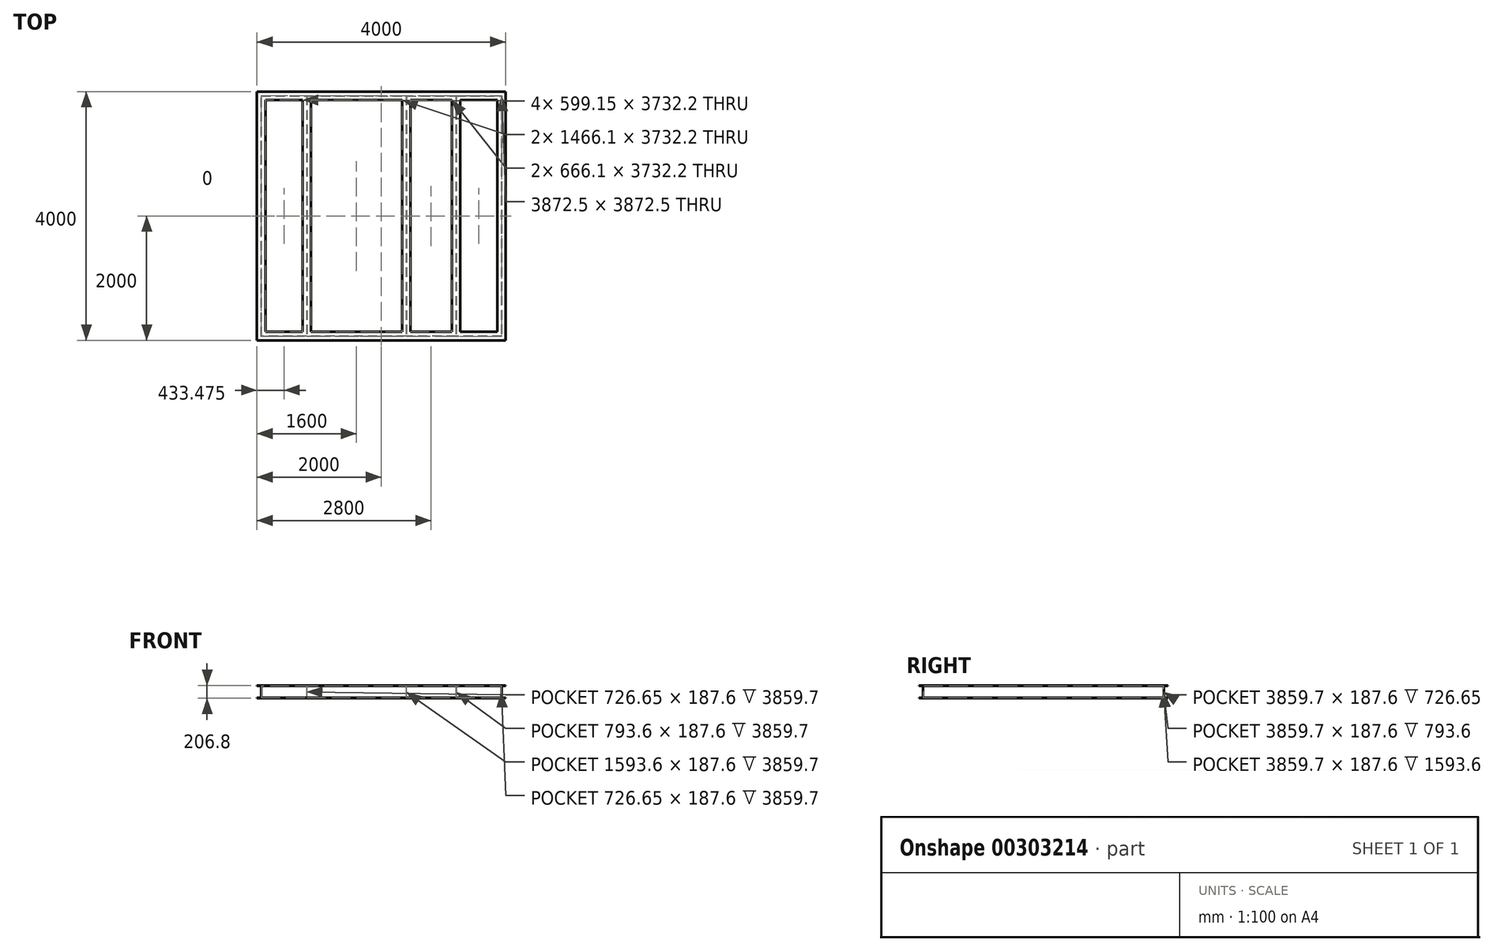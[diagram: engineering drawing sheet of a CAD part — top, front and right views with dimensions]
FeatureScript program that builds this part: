
annotation { "Feature Type Name" : "Feature", "Feature Type Description" : "" }
export const myFeature = defineFeature(function(context is Context, id is Id, definition is map)
    precondition{}
    {
        {
            var Q0;
            Q0=qCreatedBy(makeId("Top.planeOp"),FACE);
            var sketch = newSketch(context, id + "F0", { "sketchPlane" : qUnion([Q0])});
            skCircle(sketch, "E0", {"center": v(0, 0) * mm, "radius": 1985 * mm});
            skLineSegment(sketch, "E1.bottom", {"start": v(-1933.05, 1933.05) * mm, "end": v(1933.05, 1933.05) * mm});
            skLineSegment(sketch, "E1.top", {"start": v(-1933.05, -1933.05) * mm, "end": v(1933.05, -1933.05) * mm});
            skLineSegment(sketch, "E1.left", {"start": v(-1933.05, 1933.05) * mm, "end": v(-1933.05, -1933.05) * mm});
            skLineSegment(sketch, "E1.right", {"start": v(1933.05, 1933.05) * mm, "end": v(1933.05, -1933.05) * mm});
            skLineSegment(sketch, "E2", {"start": v(-1200, -1933.05) * mm, "end": v(-1200, 1933.05) * mm});
            skLineSegment(sketch, "E3", {"start": v(-400, -1933.05) * mm, "end": v(-400, 1933.05) * mm});
            skLineSegment(sketch, "E4", {"start": v(1200, -1933.05) * mm, "end": v(1200, 1933.05) * mm});
            skLineSegment(sketch, "E5", {"start": v(400, -1933.05) * mm, "end": v(400, 1933.05) * mm});
            skSolve(sketch);
        }
        {
            var Q0;
            Q0=qCreatedBy(makeId("Front.planeOp"),FACE);
            var sketch = newSketch(context, id + "F1", { "sketchPlane" : qUnion([Q0])});
            skLineSegment(sketch, "E6.bottom", {"start": v(1866.1, 103.4) * mm, "end": v(2000, 103.4) * mm});
            skLineSegment(sketch, "E6.top", {"start": v(1866.1, -103.4) * mm, "end": v(2000, -103.4) * mm});
            skLineSegment(sketch, "E6.left", {"start": v(1866.1, 103.4) * mm, "end": v(1866.1, 93.8) * mm});
            skLineSegment(sketch, "E6.right", {"start": v(2000, 103.4) * mm, "end": v(2000, 93.8) * mm});
            skLineSegment(sketch, "E7", {"start": v(1866.1, 93.8) * mm, "end": v(1929.85, 93.8) * mm});
            skLineSegment(sketch, "E8", {"start": v(1866.1, -93.8) * mm, "end": v(1929.85, -93.8) * mm});
            skLineSegment(sketch, "E9.left", {"start": v(1929.85, 93.8) * mm, "end": v(1929.85, -93.8) * mm});
            skLineSegment(sketch, "E9.right", {"start": v(1936.25, 93.8) * mm, "end": v(1936.25, -93.8) * mm});
            skLineSegment(sketch, "E10.trimOffspring", {"start": v(1936.25, -93.8) * mm, "end": v(2000, -93.8) * mm});
            skLineSegment(sketch, "E11.trimOffspring", {"start": v(2000, -93.8) * mm, "end": v(2000, -103.4) * mm});
            skLineSegment(sketch, "E12.trimOffspring", {"start": v(1866.1, -93.8) * mm, "end": v(1866.1, -103.4) * mm});
            skLineSegment(sketch, "E13.trimOffspring", {"start": v(1936.25, 93.8) * mm, "end": v(2000, 93.8) * mm});
            skLineSegment(sketch, "E14.1.0.0", {"start": v(1046.1, 103.4) * mm, "end": v(1180, 103.4) * mm});
            skLineSegment(sketch, "E14.1.0.1", {"start": v(1116.25, 93.8) * mm, "end": v(1116.25, -93.8) * mm});
            skLineSegment(sketch, "E14.1.0.2", {"start": v(1046.1, -93.8) * mm, "end": v(1109.85, -93.8) * mm});
            skLineSegment(sketch, "E14.1.0.3", {"start": v(1116.25, -93.8) * mm, "end": v(1180, -93.8) * mm});
            skLineSegment(sketch, "E14.1.0.4", {"start": v(1046.1, -103.4) * mm, "end": v(1180, -103.4) * mm});
            skLineSegment(sketch, "E14.1.0.5", {"start": v(1116.25, 93.8) * mm, "end": v(1180, 93.8) * mm});
            skLineSegment(sketch, "E14.1.0.6", {"start": v(1046.1, 93.8) * mm, "end": v(1109.85, 93.8) * mm});
            skLineSegment(sketch, "E14.1.0.7", {"start": v(1109.85, 93.8) * mm, "end": v(1109.85, -93.8) * mm});
            skLineSegment(sketch, "E14.1.0.8", {"start": v(1180, 103.4) * mm, "end": v(1180, 93.8) * mm});
            skLineSegment(sketch, "E14.1.0.9", {"start": v(1046.1, -93.8) * mm, "end": v(1046.1, -103.4) * mm});
            skLineSegment(sketch, "E14.1.0.10", {"start": v(1046.1, 103.4) * mm, "end": v(1046.1, 93.8) * mm});
            skLineSegment(sketch, "E14.1.0.11", {"start": v(1180, -93.8) * mm, "end": v(1180, -103.4) * mm});
            skLineSegment(sketch, "E14.2.0.0", {"start": v(226.1, 103.4) * mm, "end": v(360, 103.4) * mm});
            skLineSegment(sketch, "E14.2.0.1", {"start": v(296.25, 93.8) * mm, "end": v(296.25, -93.8) * mm});
            skLineSegment(sketch, "E14.2.0.2", {"start": v(226.1, -93.8) * mm, "end": v(289.85, -93.8) * mm});
            skLineSegment(sketch, "E14.2.0.3", {"start": v(296.25, -93.8) * mm, "end": v(360, -93.8) * mm});
            skLineSegment(sketch, "E14.2.0.4", {"start": v(226.1, -103.4) * mm, "end": v(360, -103.4) * mm});
            skLineSegment(sketch, "E14.2.0.5", {"start": v(296.25, 93.8) * mm, "end": v(360, 93.8) * mm});
            skLineSegment(sketch, "E14.2.0.6", {"start": v(226.1, 93.8) * mm, "end": v(289.85, 93.8) * mm});
            skLineSegment(sketch, "E14.2.0.7", {"start": v(289.85, 93.8) * mm, "end": v(289.85, -93.8) * mm});
            skLineSegment(sketch, "E14.2.0.8", {"start": v(360, 103.4) * mm, "end": v(360, 93.8) * mm});
            skLineSegment(sketch, "E14.2.0.9", {"start": v(226.1, -93.8) * mm, "end": v(226.1, -103.4) * mm});
            skLineSegment(sketch, "E14.2.0.10", {"start": v(226.1, 103.4) * mm, "end": v(226.1, 93.8) * mm});
            skLineSegment(sketch, "E14.2.0.11", {"start": v(360, -93.8) * mm, "end": v(360, -103.4) * mm});
            skLineSegment(sketch, "E14.direction1", {"start": v(1866.1, -93.8) * mm, "end": v(1046.1, -93.8) * mm, "construction": true});
            skSolve(sketch);
        }
        {
            var Q0;
            Q0=makeQuery(id+"F1.imprint","IMPRINT",FACE,{"disambiguationData":[TD([[makeQuery(id+"F1.imprint","IMPRINT",EDGE,{"derivedFrom":sQuery(id+"F1.wireOp",EDGE,"E6.bottom")}),-1.0]])]});
            var Q1;
            Q1=sQuery(id+"F0.wireOp",EDGE,"E1.top");
            var Q2;
            Q2=sQuery(id+"F0.wireOp",EDGE,"E1.right");
            var Q3;
            Q3=sQuery(id+"F0.wireOp",EDGE,"E1.left");
            var Q4;
            Q4=sQuery(id+"F0.wireOp",EDGE,"E1.bottom");
            sweep(context, id + "F2", {"profiles" : qUnion([Q0]), "path" : qUnion([Q1, Q2, Q3, Q4])});
        }
        {
            var Q0;
            Q0=makeQuery(id+"F2.opSweep","SWEPT_FACE",FACE,{"disambiguationData":[OSD([sQuery(id+"F0.wireOp",EDGE,"E1.bottom"),sQuery(id+"F1.wireOp",EDGE,"E9.right")])]});
            cPlane(context, id + "F3", {"entities" : qUnion([Q0]), "cplaneType" : CPlaneType.OFFSET, "offset" : 3.2 * mm, "oppositeDirection" : true, "width" : 150 * mm, "height" : 150 * mm});
        }
        {
            var Q0;
            Q0=qCreatedBy(id+"F3.planeOp",FACE);
            var sketch = newSketch(context, id + "F4", { "sketchPlane" : qUnion([Q0])});
            skLineSegment(sketch, "E15.bottom", {"start": v(-1866.1, 103.4) * mm, "end": v(-2000, 103.4) * mm});
            skLineSegment(sketch, "E15.top", {"start": v(-1866.1, -103.4) * mm, "end": v(-2000, -103.4) * mm});
            skLineSegment(sketch, "E15.left", {"start": v(-1866.1, 103.4) * mm, "end": v(-1866.1, 93.8) * mm});
            skLineSegment(sketch, "E15.right", {"start": v(-2000, 103.4) * mm, "end": v(-2000, 93.8) * mm});
            skLineSegment(sketch, "E16.bottom", {"start": v(-2000, 103.4) * mm, "end": v(-1866.1, 103.4) * mm});
            skLineSegment(sketch, "E16.top", {"start": v(-2000, 93.8) * mm, "end": v(-1936.25, 93.8) * mm});
            skLineSegment(sketch, "E17.left", {"start": v(-1929.85, 93.8) * mm, "end": v(-1929.85, -93.8) * mm});
            skLineSegment(sketch, "E17.right", {"start": v(-1936.25, 93.8) * mm, "end": v(-1936.25, -93.8) * mm});
            skLineSegment(sketch, "E18.bottom", {"start": v(-2000, -93.8) * mm, "end": v(-1936.25, -93.8) * mm});
            skLineSegment(sketch, "E18.top", {"start": v(-2000, -103.4) * mm, "end": v(-1866.1, -103.4) * mm});
            skLineSegment(sketch, "E18.left", {"start": v(-2000, -93.8) * mm, "end": v(-2000, -103.4) * mm});
            skLineSegment(sketch, "E18.right", {"start": v(-1866.1, -93.8) * mm, "end": v(-1866.1, -103.4) * mm});
            skLineSegment(sketch, "E19.trimOffspring", {"start": v(-1929.85, -93.8) * mm, "end": v(-1866.1, -93.8) * mm});
            skLineSegment(sketch, "E20.trimOffspring", {"start": v(-1929.85, 93.8) * mm, "end": v(-1866.1, 93.8) * mm});
            skLineSegment(sketch, "E21.1.0.0", {"start": v(-1266.95, 103.4) * mm, "end": v(-1133.05, 103.4) * mm});
            skLineSegment(sketch, "E21.1.0.1", {"start": v(-1203.2, 93.8) * mm, "end": v(-1203.2, -93.8) * mm});
            skLineSegment(sketch, "E21.1.0.2", {"start": v(-1196.8, 93.8) * mm, "end": v(-1196.8, -93.8) * mm});
            skLineSegment(sketch, "E21.1.0.3", {"start": v(-1266.95, 93.8) * mm, "end": v(-1203.2, 93.8) * mm});
            skLineSegment(sketch, "E21.1.0.4", {"start": v(-1266.95, 103.4) * mm, "end": v(-1266.95, 93.8) * mm});
            skLineSegment(sketch, "E21.1.0.5", {"start": v(-1133.05, 103.4) * mm, "end": v(-1133.05, 93.8) * mm});
            skLineSegment(sketch, "E21.1.0.6", {"start": v(-1196.8, 93.8) * mm, "end": v(-1133.05, 93.8) * mm});
            skLineSegment(sketch, "E21.1.0.7", {"start": v(-1196.8, -93.8) * mm, "end": v(-1133.05, -93.8) * mm});
            skLineSegment(sketch, "E21.1.0.8", {"start": v(-1133.05, -93.8) * mm, "end": v(-1133.05, -103.4) * mm});
            skLineSegment(sketch, "E21.1.0.9", {"start": v(-1266.95, -103.4) * mm, "end": v(-1133.05, -103.4) * mm});
            skLineSegment(sketch, "E21.1.0.10", {"start": v(-1266.95, -93.8) * mm, "end": v(-1266.95, -103.4) * mm});
            skLineSegment(sketch, "E21.1.0.11", {"start": v(-1266.95, -93.8) * mm, "end": v(-1203.2, -93.8) * mm});
            skLineSegment(sketch, "E21.direction1", {"start": v(-2000, 103.4) * mm, "end": v(-1266.95, 103.4) * mm, "construction": true});
            skLineSegment(sketch, "E22.1.0.0", {"start": v(-466.95, -103.4) * mm, "end": v(-333.05, -103.4) * mm});
            skLineSegment(sketch, "E22.1.0.1", {"start": v(-396.8, 93.8) * mm, "end": v(-396.8, -93.8) * mm});
            skLineSegment(sketch, "E22.1.0.2", {"start": v(-466.95, 103.4) * mm, "end": v(266.1, 103.4) * mm, "construction": true});
            skLineSegment(sketch, "E22.1.0.3", {"start": v(-396.8, 93.8) * mm, "end": v(-333.05, 93.8) * mm});
            skLineSegment(sketch, "E22.1.0.4", {"start": v(-396.8, -93.8) * mm, "end": v(-333.05, -93.8) * mm});
            skLineSegment(sketch, "E22.1.0.5", {"start": v(-403.2, 93.8) * mm, "end": v(-403.2, -93.8) * mm});
            skLineSegment(sketch, "E22.1.0.6", {"start": v(-466.95, -93.8) * mm, "end": v(-403.2, -93.8) * mm});
            skLineSegment(sketch, "E22.1.0.7", {"start": v(-466.95, 93.8) * mm, "end": v(-403.2, 93.8) * mm});
            skLineSegment(sketch, "E22.1.0.8", {"start": v(-466.95, 103.4) * mm, "end": v(-333.05, 103.4) * mm});
            skLineSegment(sketch, "E22.1.0.9", {"start": v(-333.05, -103.4) * mm, "end": v(-466.95, -103.4) * mm});
            skLineSegment(sketch, "E22.1.0.10", {"start": v(-333.05, 103.4) * mm, "end": v(-466.95, 103.4) * mm});
            skLineSegment(sketch, "E22.1.0.11", {"start": v(-333.05, 103.4) * mm, "end": v(-333.05, 93.8) * mm});
            skLineSegment(sketch, "E22.1.0.12", {"start": v(-466.95, -93.8) * mm, "end": v(-466.95, -103.4) * mm});
            skLineSegment(sketch, "E22.1.0.13", {"start": v(-333.05, -93.8) * mm, "end": v(-333.05, -103.4) * mm});
            skLineSegment(sketch, "E22.1.0.14", {"start": v(-333.05, -93.8) * mm, "end": v(-333.05, -103.4) * mm});
            skLineSegment(sketch, "E22.1.0.15", {"start": v(-466.95, -93.8) * mm, "end": v(-466.95, -103.4) * mm});
            skLineSegment(sketch, "E22.1.0.16", {"start": v(-333.05, 103.4) * mm, "end": v(-333.05, 93.8) * mm});
            skLineSegment(sketch, "E22.1.0.17", {"start": v(-466.95, 103.4) * mm, "end": v(-466.95, 93.8) * mm});
            skLineSegment(sketch, "E22.1.0.18", {"start": v(-466.95, 103.4) * mm, "end": v(-466.95, 93.8) * mm});
            skLineSegment(sketch, "E22.direction1", {"start": v(-2000, -103.4) * mm, "end": v(-466.95, -103.4) * mm, "construction": true});
            skLineSegment(sketch, "E23.1.0.0", {"start": v(333.05, -93.8) * mm, "end": v(333.05, -103.4) * mm});
            skLineSegment(sketch, "E23.1.0.1", {"start": v(466.95, -93.8) * mm, "end": v(466.95, -103.4) * mm});
            skLineSegment(sketch, "E23.1.0.2", {"start": v(466.95, -93.8) * mm, "end": v(466.95, -103.4) * mm});
            skLineSegment(sketch, "E23.1.0.3", {"start": v(333.05, 103.4) * mm, "end": v(333.05, 93.8) * mm});
            skLineSegment(sketch, "E23.1.0.4", {"start": v(333.05, 103.4) * mm, "end": v(333.05, 93.8) * mm});
            skLineSegment(sketch, "E23.1.0.5", {"start": v(333.05, -103.4) * mm, "end": v(1866.1, -103.4) * mm, "construction": true});
            skLineSegment(sketch, "E23.1.0.6", {"start": v(403.2, 93.8) * mm, "end": v(466.95, 93.8) * mm});
            skLineSegment(sketch, "E23.1.0.7", {"start": v(333.05, 93.8) * mm, "end": v(396.8, 93.8) * mm});
            skLineSegment(sketch, "E23.1.0.8", {"start": v(333.05, 103.4) * mm, "end": v(1066.1, 103.4) * mm, "construction": true});
            skLineSegment(sketch, "E23.1.0.9", {"start": v(403.2, -93.8) * mm, "end": v(466.95, -93.8) * mm});
            skLineSegment(sketch, "E23.1.0.10", {"start": v(396.8, 93.8) * mm, "end": v(396.8, -93.8) * mm});
            skLineSegment(sketch, "E23.1.0.11", {"start": v(333.05, -93.8) * mm, "end": v(396.8, -93.8) * mm});
            skLineSegment(sketch, "E23.1.0.12", {"start": v(403.2, 93.8) * mm, "end": v(403.2, -93.8) * mm});
            skLineSegment(sketch, "E23.1.0.13", {"start": v(333.05, -103.4) * mm, "end": v(466.95, -103.4) * mm});
            skLineSegment(sketch, "E23.1.0.14", {"start": v(333.05, 103.4) * mm, "end": v(466.95, 103.4) * mm});
            skLineSegment(sketch, "E23.1.0.15", {"start": v(466.95, 103.4) * mm, "end": v(333.05, 103.4) * mm});
            skLineSegment(sketch, "E23.1.0.16", {"start": v(466.95, -103.4) * mm, "end": v(333.05, -103.4) * mm});
            skLineSegment(sketch, "E23.1.0.17", {"start": v(466.95, 103.4) * mm, "end": v(466.95, 93.8) * mm});
            skLineSegment(sketch, "E23.1.0.18", {"start": v(466.95, 103.4) * mm, "end": v(466.95, 93.8) * mm});
            skLineSegment(sketch, "E23.1.0.19", {"start": v(333.05, -93.8) * mm, "end": v(333.05, -103.4) * mm});
            skLineSegment(sketch, "E23.direction1", {"start": v(-2000, -103.4) * mm, "end": v(333.05, -103.4) * mm, "construction": true});
            skLineSegment(sketch, "E24.1.0.0", {"start": v(1196.8, 93.8) * mm, "end": v(1196.8, -93.8) * mm});
            skLineSegment(sketch, "E24.1.0.1", {"start": v(1133.05, 103.4) * mm, "end": v(1866.1, 103.4) * mm, "construction": true});
            skLineSegment(sketch, "E24.1.0.2", {"start": v(1203.2, 93.8) * mm, "end": v(1203.2, -93.8) * mm});
            skLineSegment(sketch, "E24.1.0.3", {"start": v(1133.05, -103.4) * mm, "end": v(2666.1, -103.4) * mm, "construction": true});
            skLineSegment(sketch, "E24.1.0.4", {"start": v(1133.05, -103.4) * mm, "end": v(3466.1, -103.4) * mm, "construction": true});
            skLineSegment(sketch, "E24.1.0.5", {"start": v(1203.2, 93.8) * mm, "end": v(1266.95, 93.8) * mm});
            skLineSegment(sketch, "E24.1.0.6", {"start": v(1133.05, 103.4) * mm, "end": v(1266.95, 103.4) * mm});
            skLineSegment(sketch, "E24.1.0.7", {"start": v(1133.05, 93.8) * mm, "end": v(1196.8, 93.8) * mm});
            skLineSegment(sketch, "E24.1.0.8", {"start": v(1266.95, 103.4) * mm, "end": v(1133.05, 103.4) * mm});
            skLineSegment(sketch, "E24.1.0.9", {"start": v(1133.05, -93.8) * mm, "end": v(1196.8, -93.8) * mm});
            skLineSegment(sketch, "E24.1.0.10", {"start": v(1266.95, 103.4) * mm, "end": v(1266.95, 93.8) * mm});
            skLineSegment(sketch, "E24.1.0.11", {"start": v(1266.95, -93.8) * mm, "end": v(1266.95, -103.4) * mm});
            skLineSegment(sketch, "E24.1.0.12", {"start": v(1133.05, -103.4) * mm, "end": v(1266.95, -103.4) * mm});
            skLineSegment(sketch, "E24.1.0.13", {"start": v(1203.2, -93.8) * mm, "end": v(1266.95, -93.8) * mm});
            skLineSegment(sketch, "E24.1.0.14", {"start": v(1266.95, -93.8) * mm, "end": v(1266.95, -103.4) * mm});
            skLineSegment(sketch, "E24.1.0.15", {"start": v(1266.95, -103.4) * mm, "end": v(1133.05, -103.4) * mm});
            skLineSegment(sketch, "E24.1.0.16", {"start": v(1266.95, 103.4) * mm, "end": v(1266.95, 93.8) * mm});
            skLineSegment(sketch, "E24.1.0.17", {"start": v(1133.05, 103.4) * mm, "end": v(1133.05, 93.8) * mm});
            skLineSegment(sketch, "E24.1.0.18", {"start": v(1133.05, 103.4) * mm, "end": v(1133.05, 93.8) * mm});
            skLineSegment(sketch, "E24.1.0.19", {"start": v(1133.05, -93.8) * mm, "end": v(1133.05, -103.4) * mm});
            skLineSegment(sketch, "E24.1.0.20", {"start": v(1133.05, -93.8) * mm, "end": v(1133.05, -103.4) * mm});
            skLineSegment(sketch, "E24.direction1", {"start": v(-2000, -103.4) * mm, "end": v(1133.05, -103.4) * mm, "construction": true});
            skSolve(sketch);
        }
        {
            var Q0;
            Q0=makeQuery(id+"F4.imprint","IMPRINT",FACE,{"disambiguationData":[TD([[makeQuery(id+"F4.imprint","IMPRINT",EDGE,{"derivedFrom":sQuery(id+"F4.wireOp",EDGE,"E21.1.0.0")}),-1.0]])]});
            var Q1;
            Q1=makeQuery(id+"F4.imprint","IMPRINT",FACE,{"disambiguationData":[TD([[makeQuery(id+"F4.imprint","IMPRINT",EDGE,{"derivedFrom":sQuery(id+"F4.wireOp",EDGE,"E22.1.0.1")}),-1.0]])]});
            var Q2;
            Q2=makeQuery(id+"F4.imprint","IMPRINT",FACE,{"disambiguationData":[TD([[makeQuery(id+"F4.imprint","IMPRINT",EDGE,{"derivedFrom":sQuery(id+"F4.wireOp",EDGE,"E23.1.0.2")}),-1.0]])]});
            var Q3;
            Q3=makeQuery(id+"F4.imprint","IMPRINT",FACE,{"disambiguationData":[TD([[makeQuery(id+"F4.imprint","IMPRINT",EDGE,{"derivedFrom":sQuery(id+"F4.wireOp",EDGE,"E24.1.0.0")}),1.0]])]});
            var Q4;
            Q4=sQuery(id+"F0.wireOp",EDGE,"E3");
            var Q5;
            Q5=sQuery(id+"F0.wireOp",EDGE,"E5");
            var Q6;
            Q6=sQuery(id+"F0.wireOp",EDGE,"E4");
            var Q7;
            Q7=sQuery(id+"F0.wireOp",EDGE,"E2");
            var Q8;
            Q8=sQuery(id+"F0.wireOp",EDGE,"E4");
            sweep(context, id + "F5", {"operationType" : NewBodyOperationType.ADD, "profiles" : qUnion([Q0, Q1, Q2, Q3]), "surfaceProfiles" : qUnion([Q4, Q5, Q6, Q7]), "path" : qUnion([Q8])});
        }
    });
